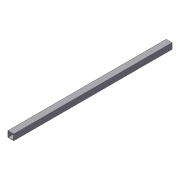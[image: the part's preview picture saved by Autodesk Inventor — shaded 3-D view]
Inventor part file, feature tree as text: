
AUTODESK INVENTOR PART (.ipt)
format: ipt  version: 2012 (Build 160160000, 160)  size: 71,168 bytes
history: native  units: in
note: dims shown in document units (in); Inventor stores cm internally (conversion verified against a paired STEP export)
features: extrude x1, shell x1, sketch x1
ambient origin geometry x8: Origin, YZ Plane, XZ Plane, XY Plane, X Axis, Y Axis, Z Axis, Center Point
bodies: Solid1 (feature_tree)
feature tree (3):
  extrude  "Extrusion1"  Depth=1.0in
  shell  "Shell1"  Thickness=27.0in
  sketch  "Sketch1"  dims[d0=1.0in d1=1.0in d2=27.0in d3=0.0in d4=0.0625in]
